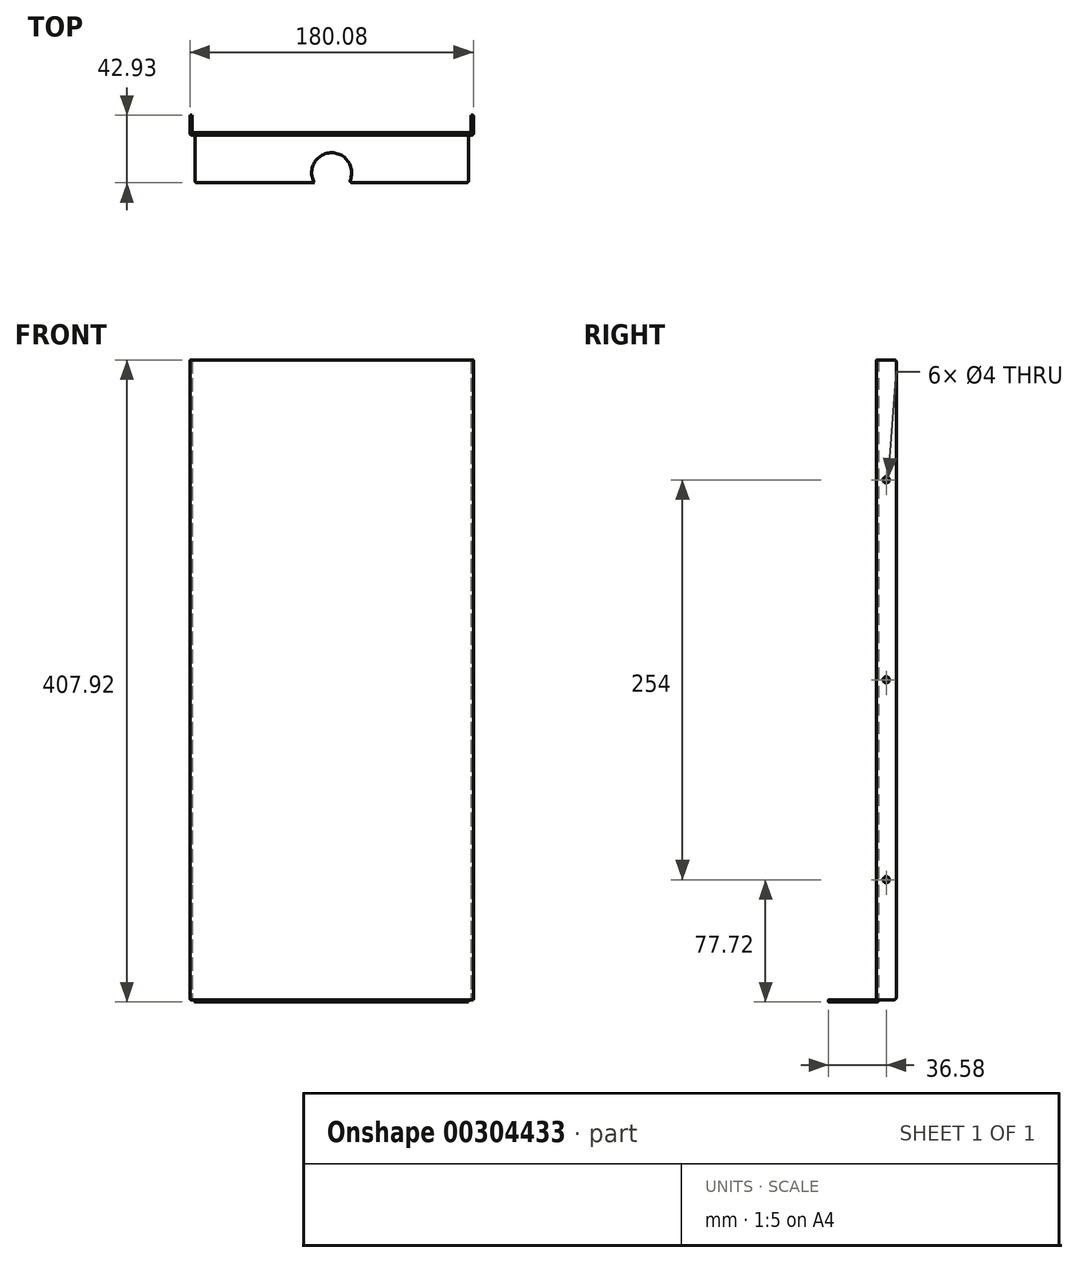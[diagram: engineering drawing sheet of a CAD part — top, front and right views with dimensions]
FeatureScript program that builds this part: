
annotation { "Feature Type Name" : "Feature", "Feature Type Description" : "" }
export const myFeature = defineFeature(function(context is Context, id is Id, definition is map)
    precondition{}
    {
        {
            var Q0;
            Q0=qCreatedBy(makeId("Front.planeOp"),FACE);
            var sketch = newSketch(context, id + "F0", { "sketchPlane" : qUnion([Q0])});
            skLineSegment(sketch, "E0.bottom", {"start": v(-90.04, 406.4) * mm, "end": v(90.04, 406.4) * mm});
            skLineSegment(sketch, "E0.top", {"start": v(-90.04, 0) * mm, "end": v(90.04, 0) * mm});
            skLineSegment(sketch, "E0.left", {"start": v(-90.04, 406.4) * mm, "end": v(-90.04, 0) * mm});
            skLineSegment(sketch, "E0.right", {"start": v(90.04, 406.4) * mm, "end": v(90.04, 0) * mm});
            skSolve(sketch);
        }
        {
            var Q0;
            Q0 = qSketchRegion(id + "F0", true);
            extrude(context, id + "F1", {"entities" : qUnion([Q0]), "oppositeDirection" : true, "depth" : 12.7 * mm, "offsetDistance" : 25.4 * mm});
        }
        {
            var Q0;
            Q0=makeQuery(id+"F1.opExtrude","SWEPT_FACE",FACE,{"disambiguationData":[OSD([sQuery(id+"F0.wireOp",EDGE,"E0.bottom")])]});
            var Q1;
            Q1=makeQuery(id+"F1.opExtrude","SWEPT_FACE",FACE,{"disambiguationData":[OSD([sQuery(id+"F0.wireOp",EDGE,"E0.top")])]});
            var Q2;
            Q2=makeQuery(id+"F1.opExtrude","CAP_FACE",FACE,{"disambiguationData":[OSD([sQuery(id+"F0.wireOp",EDGE,"E0.bottom"),sQuery(id+"F0.wireOp",EDGE,"E0.top"),sQuery(id+"F0.wireOp",EDGE,"E0.left"),sQuery(id+"F0.wireOp",EDGE,"E0.right")])],"isStart":false});
            shell(context, id + "F2", {"entities" : qUnion([Q0, Q1, Q2]), "thickness" : 1.52 * mm});
        }
        {
            var Q0;
            Q0=makeQuery(id+"F1.opExtrude","SWEPT_FACE",FACE,{"disambiguationData":[OSD([sQuery(id+"F0.wireOp",EDGE,"E0.right")])]});
            var sketch = newSketch(context, id + "F3", { "sketchPlane" : qUnion([Q0])});
            skCircle(sketch, "E1", {"center": v(6.35, 76.2) * mm, "radius": 2 * mm});
            skCircle(sketch, "E2", {"center": v(6.35, 330.2) * mm, "radius": 2 * mm});
            skCircle(sketch, "E3", {"center": v(6.35, 203.2) * mm, "radius": 2 * mm});
            skSolve(sketch);
        }
        {
            var Q0;
            Q0=qSketchRegion(id+"F3",true);
            extrude(context, id + "F4", {"entities" : qUnion([Q0]), "operationType" : NewBodyOperationType.REMOVE, "endBound" : BoundingType.THROUGH_ALL, "oppositeDirection" : true, "offsetDistance" : 25.4 * mm, "depth" : 25.4 * mm});
        }
        {
            var Q0;
            {var subQ0=sQuery(id+"F0.wireOp",EDGE,"E0.right");var subQ1=sQuery(id+"F0.wireOp",EDGE,"E0.left");var subQ2=sQuery(id+"F0.wireOp",EDGE,"E0.top");var subQ3=sQuery(id+"F0.wireOp",EDGE,"E0.bottom");Q0=makeQuery(id+"F2.opShell","OFFSET_FACE",FACE,{"disambiguationData":[OSD([subQ3,subQ2,subQ1,subQ0]),TDD([makeQuery(id+"F1.opExtrude","CAP_FACE",FACE,{"disambiguationData":[OSD([subQ3,subQ2,subQ1,subQ0])],"isStart":true})])]});}
            var sketch = newSketch(context, id + "F5", { "sketchPlane" : qUnion([Q0])});
            skLineSegment(sketch, "E4.bottom", {"start": v(-86.87, 0) * mm, "end": v(86.87, 0) * mm});
            skLineSegment(sketch, "E4.top", {"start": v(-86.87, -1.52) * mm, "end": v(86.87, -1.52) * mm});
            skLineSegment(sketch, "E4.left", {"start": v(-86.87, -1.52) * mm, "end": v(-86.87, 0) * mm});
            skLineSegment(sketch, "E4.right", {"start": v(86.87, -1.52) * mm, "end": v(86.87, 0) * mm});
            skSolve(sketch);
        }
        {
            var Q0;
            Q0 = qSketchRegion(id + "F5", true);
            extrude(context, id + "F6", {"entities" : qUnion([Q0]), "operationType" : NewBodyOperationType.ADD, "oppositeDirection" : true, "offsetDistance" : 25.4 * mm, "depth" : 31.75 * mm});
        }
        {
            var Q0;
            Q0=makeQuery(id+"F6.opExtrude","SWEPT_FACE",FACE,{"disambiguationData":[OSD([sQuery(id+"F5.wireOp",EDGE,"E4.top")])]});
            var sketch = newSketch(context, id + "F7", { "sketchPlane" : qUnion([Q0])});
            skCircle(sketch, "E5", {"center": v(0, 23.88) * mm, "radius": 12.7 * mm});
            skSolve(sketch);
        }
        {
            var Q0;
            {var subQ0=sQuery(id+"F7.wireOp",EDGE,"E5");var subQ1=makeQuery(id+"F6.opExtrude","CAP_EDGE",EDGE,{"disambiguationData":[OSD([sQuery(id+"F5.wireOp",EDGE,"E4.top")])],"isStart":false});var subQ2=makeQuery(id+"F7.imprint","INTERSECT",VERTEX,{"disambiguationData":[OD(0.0)],"derivedFrom":[subQ1,subQ0]});Q0=makeQuery(id+"F7.imprint","IMPRINT",FACE,{"disambiguationData":[TD([[makeQuery(id+"F7.imprint","IMPRINT",EDGE,{"disambiguationData":[TD([[subQ2,1.0]])],"derivedFrom":subQ0}),1.0]])]});}
            extrude(context, id + "F8", {"entities" : qUnion([Q0]), "operationType" : NewBodyOperationType.REMOVE, "oppositeDirection" : true, "offsetDistance" : 25.4 * mm, "depth" : 25.4 * mm});
        }
        {
            var Q0;
            Q0=makeQuery(id+"F1.opExtrude","CAP_EDGE",EDGE,{"disambiguationData":[OSD([sQuery(id+"F0.wireOp",EDGE,"E0.right")])],"isStart":true});
            var Q1;
            Q1=makeQuery(id+"F6.opExtrude","CAP_EDGE",EDGE,{"disambiguationData":[OSD([sQuery(id+"F5.wireOp",EDGE,"E4.top")])],"isStart":true});
            var Q2;
            Q2=makeQuery(id+"F1.opExtrude","CAP_EDGE",EDGE,{"disambiguationData":[OSD([sQuery(id+"F0.wireOp",EDGE,"E0.left")])],"isStart":true});
            var Q3;
            {var subQ0=sQuery(id+"F7.wireOp",EDGE,"E5");var subQ1=sQuery(id+"F5.wireOp",EDGE,"E4.top");Q3=makeQuery(id+"F8.boolean.opBoolean","COPY",EDGE,{"derivedFrom":makeQuery(id+"F8.opExtrude","SWEPT_EDGE",EDGE,{"disambiguationData":[OSD([subQ1,subQ0]),TDD([makeQuery(id+"F7.imprint","INTERSECT",VERTEX,{"disambiguationData":[OD(1.0)],"derivedFrom":[makeQuery(id+"F6.opExtrude","CAP_EDGE",EDGE,{"disambiguationData":[OSD([subQ1])],"isStart":false}),subQ0]})])]})});}
            var Q4;
            {var subQ0=sQuery(id+"F7.wireOp",EDGE,"E5");var subQ1=sQuery(id+"F5.wireOp",EDGE,"E4.top");Q4=makeQuery(id+"F8.boolean.opBoolean","COPY",EDGE,{"derivedFrom":makeQuery(id+"F8.opExtrude","SWEPT_EDGE",EDGE,{"disambiguationData":[OSD([subQ1,subQ0]),TDD([makeQuery(id+"F7.imprint","INTERSECT",VERTEX,{"disambiguationData":[OD(0.0)],"derivedFrom":[makeQuery(id+"F6.opExtrude","CAP_EDGE",EDGE,{"disambiguationData":[OSD([subQ1])],"isStart":false}),subQ0]})])]})});}
            var Q5;
            Q5=makeQuery(id+"F6.opExtrude","CAP_EDGE",EDGE,{"disambiguationData":[OSD([sQuery(id+"F5.wireOp",EDGE,"E4.right")])],"isStart":false});
            var Q6;
            Q6=makeQuery(id+"F6.opExtrude","CAP_EDGE",EDGE,{"disambiguationData":[OSD([sQuery(id+"F5.wireOp",EDGE,"E4.left")])],"isStart":false});
            var Q7;
            {var subQ0=sQuery(id+"F0.wireOp",EDGE,"E0.top");Q7=makeQuery(id+"F2.opShell","OFFSET_EDGE",EDGE,{"disambiguationData":[OSD([subQ0]),TDD([makeQuery(id+"F1.opExtrude","CAP_EDGE",EDGE,{"disambiguationData":[OSD([subQ0])],"isStart":false})])]});}
            var Q8;
            Q8=makeQuery(id+"F1.opExtrude","CAP_EDGE",EDGE,{"disambiguationData":[OSD([sQuery(id+"F0.wireOp",EDGE,"E0.top")])],"isStart":false});
            var Q9;
            {var subQ0=sQuery(id+"F0.wireOp",EDGE,"E0.bottom");Q9=makeQuery(id+"F2.opShell","OFFSET_EDGE",EDGE,{"disambiguationData":[OSD([subQ0]),TDD([makeQuery(id+"F1.opExtrude","CAP_EDGE",EDGE,{"disambiguationData":[OSD([subQ0])],"isStart":false})])]});}
            var Q10;
            Q10=makeQuery(id+"F1.opExtrude","CAP_EDGE",EDGE,{"disambiguationData":[OSD([sQuery(id+"F0.wireOp",EDGE,"E0.bottom")])],"isStart":false});
            fillet(context, id + "F9", {"entities" : qUnion([Q0, Q1, Q2, Q3, Q4, Q5, Q6, Q7, Q8, Q9, Q10]), "tangentPropagation" : true, "radius" : 1.27 * mm, "defaultsChanged" : false, "vertexSettings" : [], "allowEdgeOverflow" : false});
        }
        {
            var Q0;
            {var subQ0=sQuery(id+"F0.wireOp",EDGE,"E0.left");Q0=makeQuery(id+"F2.opShell","OFFSET_EDGE",EDGE,{"disambiguationData":[OSD([subQ0]),TDD([makeQuery(id+"F1.opExtrude","CAP_EDGE",EDGE,{"disambiguationData":[OSD([subQ0])],"isStart":true})])]});}
            var Q1;
            {var subQ0=sQuery(id+"F0.wireOp",EDGE,"E0.right");Q1=makeQuery(id+"F2.opShell","OFFSET_EDGE",EDGE,{"disambiguationData":[OSD([subQ0]),TDD([makeQuery(id+"F1.opExtrude","CAP_EDGE",EDGE,{"disambiguationData":[OSD([subQ0])],"isStart":true})])]});}
            var Q2;
            {var subQ0=sQuery(id+"F0.wireOp",EDGE,"E0.top");Q2=makeQuery(id+"F6.boolean.opBoolean","SPLIT",EDGE,{"disambiguationData":[topologyDisambiguationEdgeConnected([makeQuery(id+"F1.opExtrude","CAP_FACE",FACE,{"disambiguationData":[OSD([sQuery(id+"F0.wireOp",EDGE,"E0.bottom"),subQ0,sQuery(id+"F0.wireOp",EDGE,"E0.left"),sQuery(id+"F0.wireOp",EDGE,"E0.right")])],"isStart":true}),makeQuery(id+"F6.opExtrude","SWEPT_FACE",FACE,{"disambiguationData":[OSD([sQuery(id+"F5.wireOp",EDGE,"E4.bottom")])]})])],"derivedFrom":makeQuery(id+"F1.opExtrude","CAP_EDGE",EDGE,{"disambiguationData":[OSD([subQ0])],"isStart":true})});}
            fillet(context, id + "F10", {"entities" : qUnion([Q0, Q1, Q2]), "tangentPropagation" : true, "radius" : 0.5 * mm, "defaultsChanged" : false, "vertexSettings" : [], "allowEdgeOverflow" : false});
        }
    });
